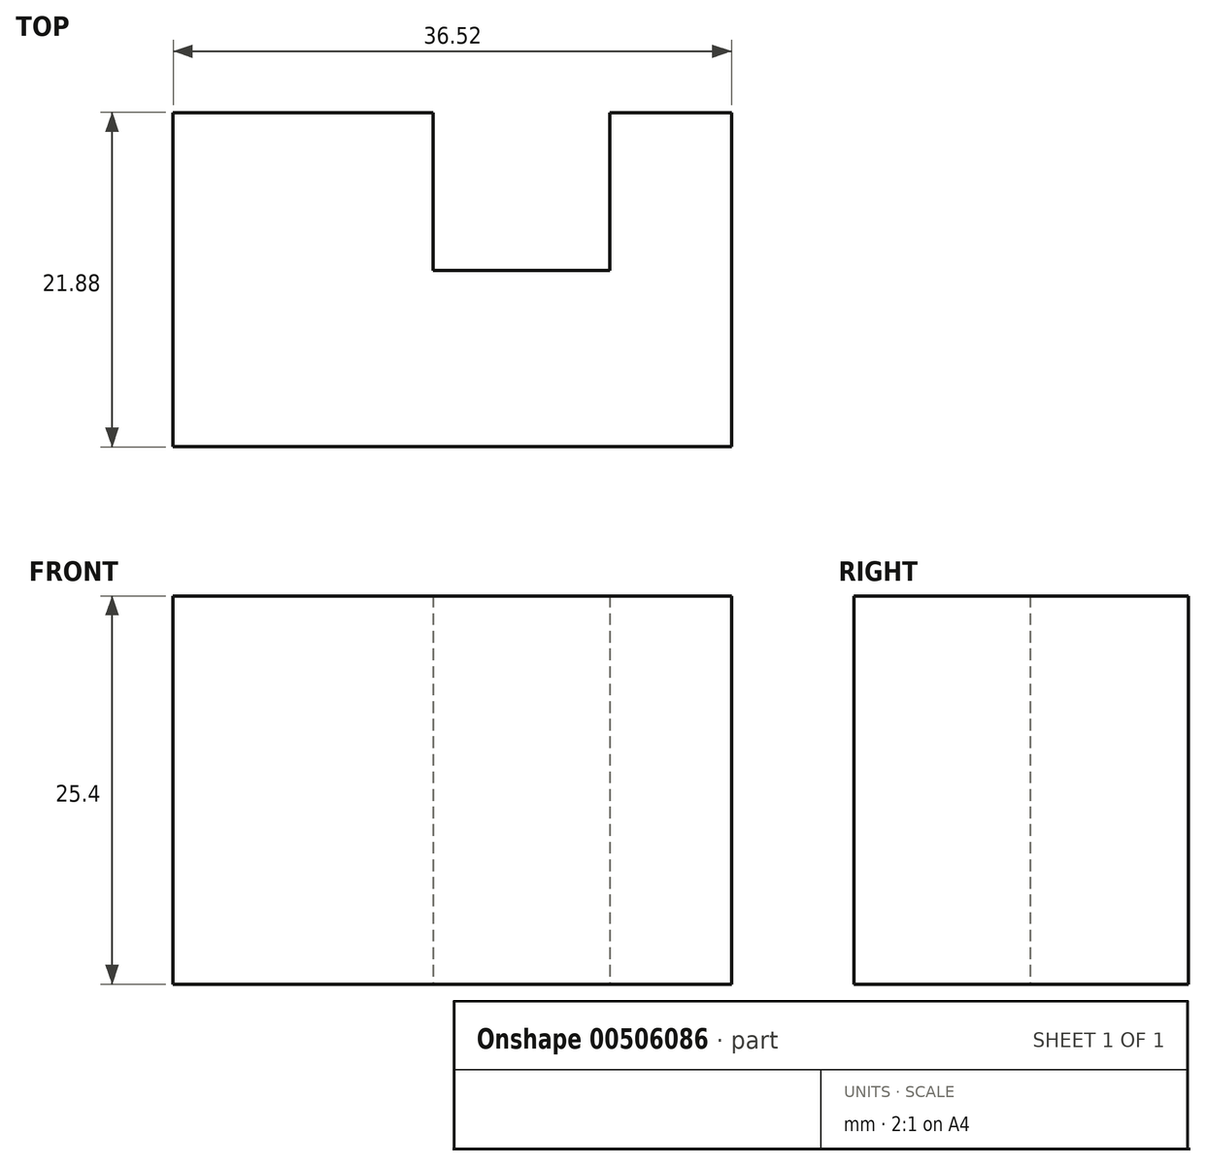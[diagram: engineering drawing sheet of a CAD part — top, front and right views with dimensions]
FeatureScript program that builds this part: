
annotation { "Feature Type Name" : "Feature", "Feature Type Description" : "" }
export const myFeature = defineFeature(function(context is Context, id is Id, definition is map)
    precondition{}
    {
        {
            var Q0;
            Q0=qCreatedBy(makeId("Top.planeOp"),FACE);
            var sketch = newSketch(context, id + "F0", { "sketchPlane" : qUnion([Q0])});
            skLineSegment(sketch, "E0.bottom", {"start": v(10.44, 13.75) * mm, "end": v(2.47, 13.75) * mm});
            skLineSegment(sketch, "E0.top", {"start": v(10.44, -8.13) * mm, "end": v(-26.08, -8.13) * mm});
            skLineSegment(sketch, "E0.left", {"start": v(10.44, 13.75) * mm, "end": v(10.44, -8.13) * mm});
            skLineSegment(sketch, "E0.right", {"start": v(-26.08, 13.75) * mm, "end": v(-26.08, -8.13) * mm});
            skLineSegment(sketch, "E1.bottom", {"start": v(-9.08, 3.4) * mm, "end": v(2.47, 3.4) * mm});
            skLineSegment(sketch, "E1.top", {"start": v(-9.08, 15.83) * mm, "end": v(2.47, 15.83) * mm, "construction": true});
            skLineSegment(sketch, "E1.left", {"start": v(-9.08, 3.4) * mm, "end": v(-9.08, 15.83) * mm});
            skLineSegment(sketch, "E1.right", {"start": v(2.47, 3.4) * mm, "end": v(2.47, 15.83) * mm});
            skArc(sketch, "E2", {"start": v(2.46, 15.83) * mm, "mid": v(-3.3, 21.59) * mm, "end": v(-9.07, 15.83) * mm});
            skLineSegment(sketch, "E3.trimOffspring", {"start": v(-9.08, 13.75) * mm, "end": v(-26.08, 13.75) * mm});
            skSolve(sketch);
        }
        {
            var Q0;
            Q0 = qSketchRegion(id + "F0", true);
            extrude(context, id + "F1", {"entities" : qUnion([Q0]), "depth" : 25.4 * mm});
        }
    });
